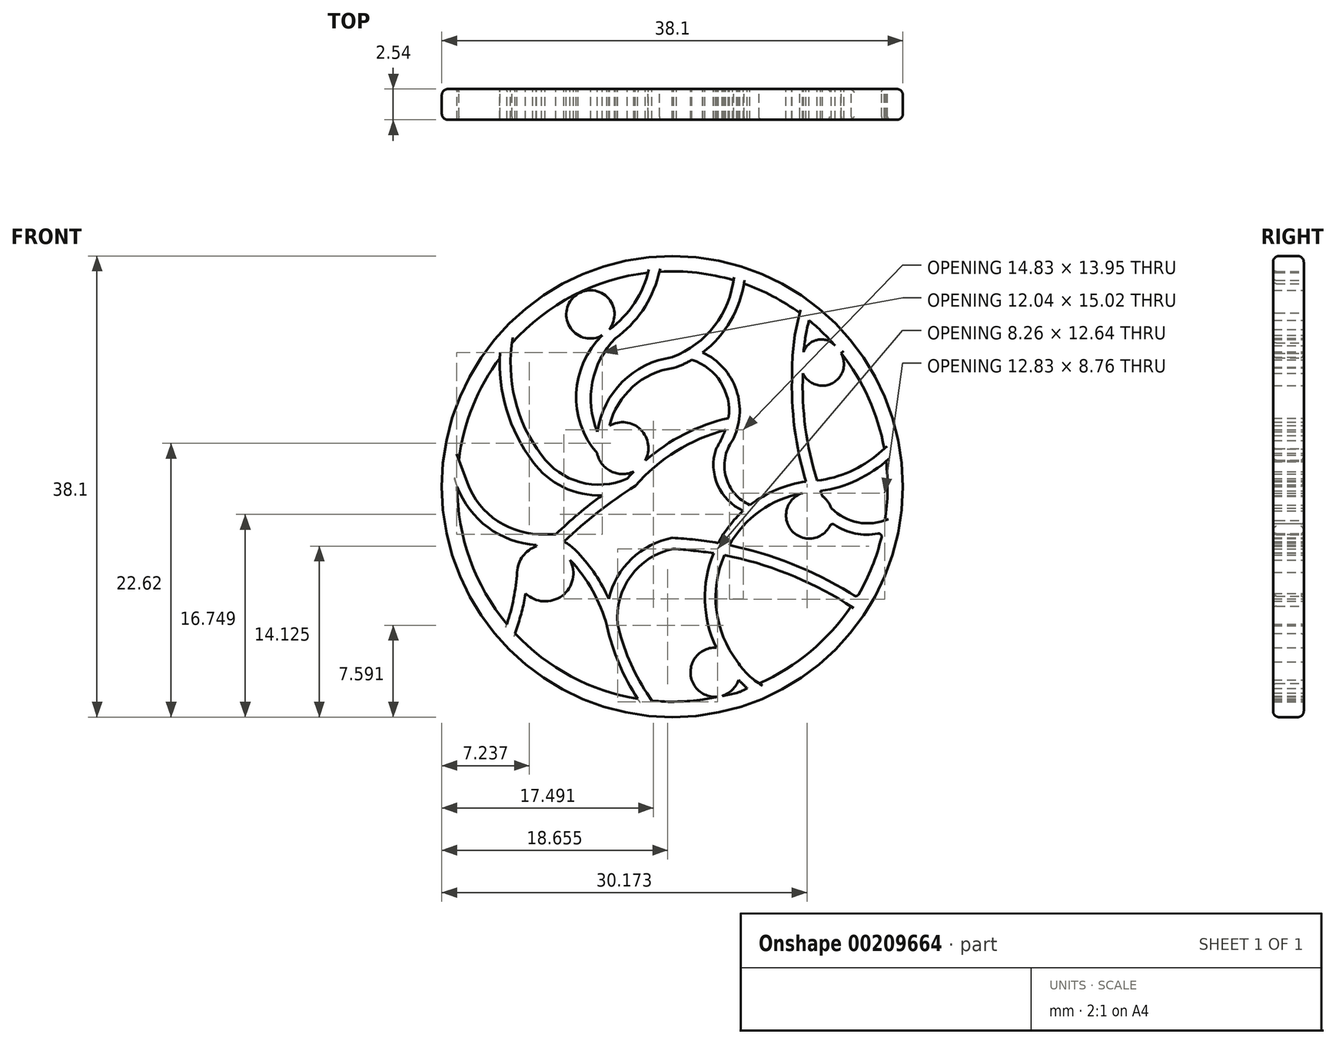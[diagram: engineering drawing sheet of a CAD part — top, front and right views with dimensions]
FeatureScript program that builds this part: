
annotation { "Feature Type Name" : "Feature", "Feature Type Description" : "" }
export const myFeature = defineFeature(function(context is Context, id is Id, definition is map)
    precondition{}
    {
        {
            var Q0;
            Q0=qCreatedBy(makeId("Front.planeOp"),FACE);
            var sketch = newSketch(context, id + "F0", { "sketchPlane" : qUnion([Q0])});
            skCircle(sketch, "E0", {"center": v(0, 0) * mm, "radius": 19.05 * mm});
            skArc(sketch, "E1.0", {"start": v(-13, -12.13) * mm, "mid": v(-8.38, -15.68) * mm, "end": v(-2.86, -17.55) * mm});
            skArc(sketch, "E2", {"start": v(-5.22, 12.98) * mm, "mid": v(-8.08, 15.73) * mm, "end": v(-5.78, 12.5) * mm});
            skArc(sketch, "E3", {"start": v(10.79, 9.34) * mm, "mid": v(13.22, 8.54) * mm, "end": v(13.94, 11) * mm});
            skArc(sketch, "E4", {"start": v(-6.22, 2.75) * mm, "mid": v(-5.07, 1.25) * mm, "end": v(-3.18, 1.24) * mm});
            skArc(sketch, "E5", {"start": v(-11.22, -4.94) * mm, "mid": v(-12.36, -5.76) * mm, "end": v(-12.83, -7.08) * mm});
            skArc(sketch, "E6", {"start": v(3.63, -13.3) * mm, "mid": v(1.5, -15.4) * mm, "end": v(3.74, -17.37) * mm});
            skArc(sketch, "E7", {"start": v(10.75, -0.55) * mm, "mid": v(9.94, -3.73) * mm, "end": v(13.14, -2.96) * mm});
            skArc(sketch, "E8", {"start": v(10.75, -0.55) * mm, "mid": v(7.25, -2.02) * mm, "end": v(4.7, -4.84) * mm});
            skArc(sketch, "E9", {"start": v(5.38, -14.47) * mm, "mid": v(6.17, -15.47) * mm, "end": v(7.16, -16.28) * mm});
            skArc(sketch, "E10", {"start": v(-13.67, -11.36) * mm, "mid": v(-13.11, -9.25) * mm, "end": v(-12.83, -7.08) * mm});
            skArc(sketch, "E11", {"start": v(-5.4, -11.52) * mm, "mid": v(-6.6, -8.6) * mm, "end": v(-8.45, -6.06) * mm});
            skArc(sketch, "E12", {"start": v(-5.4, -11.52) * mm, "mid": v(-4.4, -14.65) * mm, "end": v(-2.86, -17.55) * mm});
            skArc(sketch, "E13", {"start": v(14.79, -8.86) * mm, "mid": v(9.92, -6.4) * mm, "end": v(4.7, -4.84) * mm});
            skArc(sketch, "E14", {"start": v(0, -4.24) * mm, "mid": v(-3.38, -5.98) * mm, "end": v(-5.26, -9.28) * mm});
            skPoint(sketch, "E15.start.orphan", {"position": v(10.79, 10.89) * mm});
            skArc(sketch, "E16", {"start": v(10.79, 9.34) * mm, "mid": v(10.99, 4.86) * mm, "end": v(11.95, 0.49) * mm});
            skArc(sketch, "E17", {"start": v(13.13, -1.8) * mm, "mid": v(15.2, -2.94) * mm, "end": v(17.56, -2.8) * mm});
            skArc(sketch, "E18", {"start": v(11.3, 13.73) * mm, "mid": v(11, 12.37) * mm, "end": v(10.83, 10.98) * mm});
            skArc(sketch, "E19", {"start": v(0, 10.68) * mm, "mid": v(3.4, 13.18) * mm, "end": v(5.05, 17.05) * mm});
            skArc(sketch, "E20", {"start": v(0, 10.68) * mm, "mid": v(-4.13, 8.65) * mm, "end": v(-6.2, 4.53) * mm});
            skArc(sketch, "E21", {"start": v(4.18, 4.21) * mm, "mid": v(4.29, 4.44) * mm, "end": v(4.39, 4.68) * mm});
            skArc(sketch, "E22", {"start": v(3.6, 3.1) * mm, "mid": v(3.74, 0.11) * mm, "end": v(5.86, -2) * mm});
            skArc(sketch, "E23", {"start": v(-17.78, 0) * mm, "mid": v(-15.24, -3.38) * mm, "end": v(-11.26, -4.83) * mm});
            skArc(sketch, "E24", {"start": v(-10.82, 2.59) * mm, "mid": v(-7.62, 0.37) * mm, "end": v(-3.74, 0.64) * mm});
            skArc(sketch, "E25", {"start": v(-13.26, 11.85) * mm, "mid": v(-12.96, 6.98) * mm, "end": v(-10.82, 2.59) * mm});
            skArc(sketch, "E26", {"start": v(-5.22, 12.98) * mm, "mid": v(-3.2, 15.04) * mm, "end": v(-2.01, 17.67) * mm});
            skArc(sketch, "E27", {"start": v(-5.78, 12.5) * mm, "mid": v(-7.95, 7.71) * mm, "end": v(-6.22, 2.75) * mm});
            skArc(sketch, "E28.0", {"start": v(-4.7, 12.26) * mm, "mid": v(-2.47, 14.54) * mm, "end": v(-1.15, 17.44) * mm});
            skArc(sketch, "E29.0", {"start": v(0.12, 9.8) * mm, "mid": v(-3.28, 8.23) * mm, "end": v(-5.2, 5.02) * mm});
            skArc(sketch, "E30.0", {"start": v(0.32, 9.85) * mm, "mid": v(0.98, 10.14) * mm, "end": v(1.6, 10.47) * mm});
            skLineSegment(sketch, "E31", {"start": v(0.12, 9.8) * mm, "end": v(0.32, 9.85) * mm});
            skArc(sketch, "E32.0", {"start": v(4.96, 3.8) * mm, "mid": v(5.29, 7.96) * mm, "end": v(2.5, 11.07) * mm});
            skArc(sketch, "E33", {"start": v(4.96, 3.8) * mm, "mid": v(4.43, 0.79) * mm, "end": v(6.41, -1.54) * mm});
            skArc(sketch, "E34.trimOffspring", {"start": v(2.5, 11.07) * mm, "mid": v(4.76, 13.6) * mm, "end": v(5.91, 16.77) * mm});
            skArc(sketch, "E35.0", {"start": v(9.9, 9.35) * mm, "mid": v(10.1, 4.83) * mm, "end": v(11.05, 0.4) * mm});
            skArc(sketch, "E36.0", {"start": v(10.43, 13.95) * mm, "mid": v(10, 11.67) * mm, "end": v(9.9, 9.35) * mm});
            skArc(sketch, "E37", {"start": v(-4.7, 12.26) * mm, "mid": v(-6.61, 8.62) * mm, "end": v(-6.2, 4.53) * mm});
            skArc(sketch, "E38.0", {"start": v(-14.25, 10.63) * mm, "mid": v(-13.63, 6.11) * mm, "end": v(-11.53, 2.06) * mm});
            skArc(sketch, "E39.0", {"start": v(-11.53, 2.06) * mm, "mid": v(-9.01, -0.06) * mm, "end": v(-5.8, -0.73) * mm});
            skArc(sketch, "E40.trimOffspring", {"start": v(-5.8, -0.73) * mm, "mid": v(-7.77, -2.26) * mm, "end": v(-9.62, -3.94) * mm});
            skLineSegment(sketch, "E41", {"start": v(-1.15, 17.44) * mm, "end": v(-1.07, 17.75) * mm});
            skArc(sketch, "E42.0", {"start": v(-12.9, -11.84) * mm, "mid": v(-12.45, -10.35) * mm, "end": v(-12.13, -8.82) * mm});
            skLineSegment(sketch, "E43", {"start": v(-12.9, -11.84) * mm, "end": v(-13, -12.13) * mm});
            skArc(sketch, "E44.trimOffspring", {"start": v(-12.13, -8.82) * mm, "mid": v(-9.1, -9.02) * mm, "end": v(-8.45, -6.06) * mm});
            skArc(sketch, "E45.trimOffspring", {"start": v(-14.25, 10.63) * mm, "mid": v(-16.5, 6.63) * mm, "end": v(-17.65, 2.18) * mm});
            skArc(sketch, "E46.trimOffspring", {"start": v(-2.01, 17.67) * mm, "mid": v(-8.17, 15.8) * mm, "end": v(-13.26, 11.85) * mm});
            skArc(sketch, "E47.trimOffspring", {"start": v(5.05, 17.05) * mm, "mid": v(2.02, 17.66) * mm, "end": v(-1.07, 17.75) * mm});
            skLineSegment(sketch, "E48", {"start": v(10.43, 13.95) * mm, "end": v(10.52, 14.33) * mm});
            skArc(sketch, "E49.trimOffspring", {"start": v(10.52, 14.33) * mm, "mid": v(8.3, 15.72) * mm, "end": v(5.91, 16.77) * mm});
            skArc(sketch, "E50.0", {"start": v(11.95, 0.49) * mm, "mid": v(14.68, 1.24) * mm, "end": v(17.07, 2.76) * mm});
            skArc(sketch, "E51.0", {"start": v(11.05, 0.4) * mm, "mid": v(8.6, -0.26) * mm, "end": v(6.41, -1.54) * mm});
            skArc(sketch, "E52", {"start": v(5.47, -15.98) * mm, "mid": v(5.82, -16.33) * mm, "end": v(6.2, -16.67) * mm});
            skArc(sketch, "E53.trimOffspring", {"start": v(7.16, -16.28) * mm, "mid": v(11.42, -13.63) * mm, "end": v(14.77, -9.9) * mm});
            skArc(sketch, "E54.0", {"start": v(14.32, -9.62) * mm, "mid": v(9.48, -7.19) * mm, "end": v(4.3, -5.67) * mm});
            skArc(sketch, "E55.0", {"start": v(0.06, -5.14) * mm, "mid": v(-3.42, -7.38) * mm, "end": v(-4.52, -11.38) * mm});
            skArc(sketch, "E56.0", {"start": v(-4.52, -11.38) * mm, "mid": v(-3.58, -14.33) * mm, "end": v(-2.11, -17.06) * mm});
            skArc(sketch, "E57.trimOffspring", {"start": v(4.3, -5.67) * mm, "mid": v(3.64, -10.22) * mm, "end": v(5.38, -14.47) * mm});
            skArc(sketch, "E58.trimOffspring", {"start": v(3.79, -4.67) * mm, "mid": v(1.9, -4.4) * mm, "end": v(0, -4.24) * mm});
            skArc(sketch, "E59.trimOffspring", {"start": v(3.4, -5.5) * mm, "mid": v(2.69, -9.43) * mm, "end": v(3.63, -13.3) * mm});
            skLineSegment(sketch, "E60", {"start": v(-2.11, -17.06) * mm, "end": v(-1.7, -17.7) * mm});
            skArc(sketch, "E61.trimOffspring", {"start": v(-1.7, -17.7) * mm, "mid": v(0.43, -17.77) * mm, "end": v(2.54, -17.6) * mm});
            skArc(sketch, "E62.0", {"start": v(-16.94, 0.3) * mm, "mid": v(-14.43, -2.86) * mm, "end": v(-10.53, -3.94) * mm});
            skArc(sketch, "E63.0", {"start": v(-5.26, -9.28) * mm, "mid": v(-6.36, -7.27) * mm, "end": v(-7.78, -5.48) * mm});
            skLineSegment(sketch, "E64", {"start": v(-16.94, 0.3) * mm, "end": v(-17.65, 2.18) * mm});
            skLineSegment(sketch, "E65", {"start": v(-10.53, -3.94) * mm, "end": v(-9.62, -3.94) * mm});
            skArc(sketch, "E66", {"start": v(-7.78, -5.48) * mm, "mid": v(-8.34, -4.96) * mm, "end": v(-8.97, -4.55) * mm});
            skArc(sketch, "E67.trimOffspring", {"start": v(-17.78, 0) * mm, "mid": v(-16.72, -6.04) * mm, "end": v(-13.67, -11.36) * mm});
            skArc(sketch, "E68.trimOffspring", {"start": v(5.86, -2) * mm, "mid": v(4.7, -3.25) * mm, "end": v(3.79, -4.67) * mm});
            skArc(sketch, "E69.trimOffspring", {"start": v(12.24, -0.37) * mm, "mid": v(12.31, -0.59) * mm, "end": v(12.4, -0.8) * mm});
            skArc(sketch, "E70.trimOffspring", {"start": v(12.24, -0.37) * mm, "mid": v(15.13, 0.46) * mm, "end": v(17.66, 2.09) * mm});
            skArc(sketch, "E71.trimOffspring", {"start": v(13.13, -1.8) * mm, "mid": v(12.85, -1.24) * mm, "end": v(12.4, -0.8) * mm});
            skArc(sketch, "E72.trimOffspring", {"start": v(17.56, -2.8) * mm, "mid": v(17.78, -0.36) * mm, "end": v(17.66, 2.09) * mm});
            skLineSegment(sketch, "E73", {"start": v(17.07, 2.76) * mm, "end": v(17.5, 3.13) * mm});
            skArc(sketch, "E74.trimOffspring", {"start": v(17.5, 3.13) * mm, "mid": v(16.21, 7.3) * mm, "end": v(13.95, 11.02) * mm});
            skArc(sketch, "E75", {"start": v(13.14, -2.96) * mm, "mid": v(15.15, -3.9) * mm, "end": v(17.37, -3.79) * mm});
            skPoint(sketch, "E76.orphan", {"position": v(15.24, -9.15) * mm});
            skLineSegment(sketch, "E77", {"start": v(14.32, -9.62) * mm, "end": v(14.77, -9.9) * mm});
            skLineSegment(sketch, "E78", {"start": v(14.79, -8.86) * mm, "end": v(15.24, -9.15) * mm});
            skArc(sketch, "E79.trimOffspring", {"start": v(15.24, -9.15) * mm, "mid": v(16.53, -6.56) * mm, "end": v(17.37, -3.79) * mm});
            skPoint(sketch, "E80.start.orphan", {"position": v(11.3, -0.46) * mm});
            skLineSegment(sketch, "E81", {"start": v(0, 19.05) * mm, "end": v(0, 1.65) * mm});
            skLineSegment(sketch, "E82", {"start": v(13.95, 11.02) * mm, "end": v(13.94, 11) * mm});
            skArc(sketch, "E83", {"start": v(13.44, 11.64) * mm, "mid": v(11.88, 12.1) * mm, "end": v(10.79, 10.89) * mm});
            skArc(sketch, "E84.trimOffspring", {"start": v(13.44, 11.64) * mm, "mid": v(12.41, 12.73) * mm, "end": v(11.3, 13.73) * mm});
            skArc(sketch, "E85", {"start": v(5.32, -17.06) * mm, "mid": v(5.77, -16.89) * mm, "end": v(6.2, -16.67) * mm});
            skLineSegment(sketch, "E86", {"start": v(2.54, -17.6) * mm, "end": v(3.74, -17.37) * mm});
            skLineSegment(sketch, "E87.trimOffspring", {"start": v(4.1, -17.3) * mm, "end": v(5.32, -17.06) * mm});
            skArc(sketch, "E88.trimOffspring", {"start": v(4.1, -17.3) * mm, "mid": v(4.95, -16.8) * mm, "end": v(5.47, -15.98) * mm});
            skPoint(sketch, "E89.orphan", {"position": v(-10.5, -4.83) * mm});
            skLineSegment(sketch, "E90", {"start": v(-11.26, -4.83) * mm, "end": v(-11.22, -4.94) * mm});
            skLineSegment(sketch, "E91.trimOffspring", {"start": v(13.94, 11) * mm, "end": v(13.95, 11.02) * mm});
            skArc(sketch, "E92", {"start": v(3.4, -5.5) * mm, "mid": v(1.74, -5.3) * mm, "end": v(0.06, -5.14) * mm});
            skPoint(sketch, "E93.start.orphan", {"position": v(19.05, 0) * mm});
            skArc(sketch, "E94", {"start": v(4.64, 5.65) * mm, "mid": v(0.98, 4.32) * mm, "end": v(-2.24, 2.14) * mm});
            skArc(sketch, "E95.0", {"start": v(4.39, 4.68) * mm, "mid": v(0.31, 2.92) * mm, "end": v(-3.07, 0.06) * mm});
            skArc(sketch, "E96", {"start": v(-3.07, 0.06) * mm, "mid": v(-6.13, -2.1) * mm, "end": v(-8.97, -4.55) * mm});
            skArc(sketch, "E97", {"start": v(3.6, 3.1) * mm, "mid": v(3.91, 3.64) * mm, "end": v(4.18, 4.21) * mm});
            skArc(sketch, "E98.trimOffspring", {"start": v(4.64, 5.65) * mm, "mid": v(4, 8.62) * mm, "end": v(1.6, 10.47) * mm});
            skArc(sketch, "E99.trimOffspring", {"start": v(-3.18, 1.24) * mm, "mid": v(-3.47, 0.95) * mm, "end": v(-3.74, 0.64) * mm});
            skArc(sketch, "E100.trimOffspring", {"start": v(-2.24, 2.14) * mm, "mid": v(-2.62, 4.7) * mm, "end": v(-5.2, 5.02) * mm});
            skSolve(sketch);
        }
        {
            var Q0;
            Q0=makeQuery(id+"F0.imprint","IMPRINT",FACE,{"disambiguationData":[TD([[makeQuery(id+"F0.imprint","IMPRINT",EDGE,{"derivedFrom":sQuery(id+"F0.wireOp",EDGE,"E0")}),1.0]])]});
            extrude(context, id + "F1", {"entities" : qUnion([Q0]), "depth" : 2.54 * mm});
        }
        {
            var Q0;
            Q0=makeQuery(id+"F1.opExtrude","CAP_EDGE",EDGE,{"disambiguationData":[OSD([sQuery(id+"F0.wireOp",EDGE,"E0")])],"isStart":false});
            var Q1;
            Q1=makeQuery(id+"F1.opExtrude","CAP_EDGE",EDGE,{"disambiguationData":[OSD([sQuery(id+"F0.wireOp",EDGE,"E0")])],"isStart":true});
            fillet(context, id + "F2", {"entities" : qUnion([Q0, Q1]), "radius" : 0.5 * mm, "tangentPropagation" : true, "allowEdgeOverflow" : false});
        }
        {
            var Q0;
            Q0=makeQuery(id+"F1.opExtrude","CAP_EDGE",EDGE,{"disambiguationData":[OSD([sQuery(id+"F0.wireOp",EDGE,"E53.trimOffspring")])],"isStart":false});
            var Q1;
            Q1=makeQuery(id+"F1.opExtrude","CAP_EDGE",EDGE,{"disambiguationData":[OSD([sQuery(id+"F0.wireOp",EDGE,"E1.0")])],"isStart":true});
            var Q2;
            Q2=makeQuery(id+"F1.opExtrude","CAP_EDGE",EDGE,{"disambiguationData":[OSD([sQuery(id+"F0.wireOp",EDGE,"E67.trimOffspring")])],"isStart":true});
            var Q3;
            Q3=makeQuery(id+"F1.opExtrude","CAP_EDGE",EDGE,{"disambiguationData":[OSD([sQuery(id+"F0.wireOp",EDGE,"E45.trimOffspring")])],"isStart":true});
            var Q4;
            Q4=makeQuery(id+"F1.opExtrude","CAP_EDGE",EDGE,{"disambiguationData":[OSD([sQuery(id+"F0.wireOp",EDGE,"E45.trimOffspring")])],"isStart":false});
            var Q5;
            Q5=makeQuery(id+"F1.opExtrude","CAP_EDGE",EDGE,{"disambiguationData":[OSD([sQuery(id+"F0.wireOp",EDGE,"E46.trimOffspring")])],"isStart":false});
            var Q6;
            Q6=makeQuery(id+"F1.opExtrude","CAP_EDGE",EDGE,{"disambiguationData":[OSD([sQuery(id+"F0.wireOp",EDGE,"E47.trimOffspring")])],"isStart":false});
            var Q7;
            Q7=makeQuery(id+"F1.opExtrude","CAP_EDGE",EDGE,{"disambiguationData":[OSD([sQuery(id+"F0.wireOp",EDGE,"E49.trimOffspring")])],"isStart":false});
            var Q8;
            Q8=makeQuery(id+"F1.opExtrude","CAP_EDGE",EDGE,{"disambiguationData":[OSD([sQuery(id+"F0.wireOp",EDGE,"E74.trimOffspring")])],"isStart":false});
            var Q9;
            Q9=makeQuery(id+"F1.opExtrude","CAP_EDGE",EDGE,{"disambiguationData":[OSD([sQuery(id+"F0.wireOp",EDGE,"E72.trimOffspring")])],"isStart":false});
            var Q10;
            Q10=makeQuery(id+"F1.opExtrude","SWEPT_FACE",FACE,{"disambiguationData":[OSD([sQuery(id+"F0.wireOp",EDGE,"E79.trimOffspring")])]});
            var Q11;
            Q11=makeQuery(id+"F1.opExtrude","SWEPT_FACE",FACE,{"disambiguationData":[OSD([sQuery(id+"F0.wireOp",EDGE,"E75")])]});
            var Q12;
            Q12=makeQuery(id+"F1.opExtrude","CAP_EDGE",EDGE,{"disambiguationData":[OSD([sQuery(id+"F0.wireOp",EDGE,"E79.trimOffspring")])],"isStart":false});
            fillet(context, id + "F3", {"entities" : qUnion([Q0, Q1, Q2, Q3, Q4, Q5, Q6, Q7, Q8, Q9, Q10, Q11, Q12]), "radius" : 0.25 * mm, "tangentPropagation" : true, "allowEdgeOverflow" : false});
        }
    });
